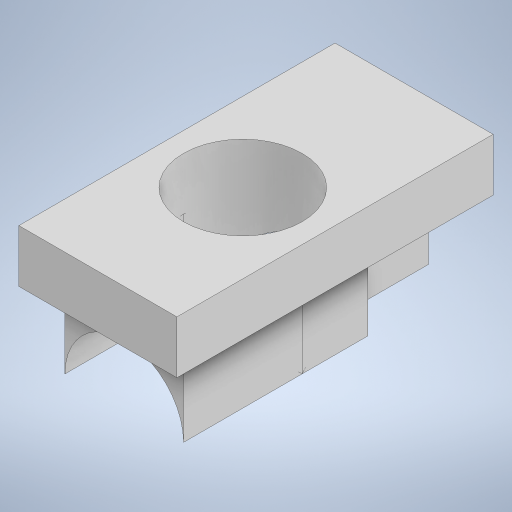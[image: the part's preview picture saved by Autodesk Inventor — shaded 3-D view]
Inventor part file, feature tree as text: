
AUTODESK INVENTOR PART (.ipt)
format: ipt  version: 2023 (Build 270158000, 158)  size: 335,872 bytes
history: native  units: in
note: dims shown in document units (in); Inventor stores cm internally (conversion verified against a paired STEP export)
features: extrude x6, plane x6, sketch x5, projected_geometry x1
ambient origin geometry x8: Origin, YZ Plane, XZ Plane, XY Plane, X Axis, Y Axis, Z Axis, Center Point
bodies: Solid1 (feature_tree)
feature tree (18):
  sketch  "Sketch1"  dims[d0=2.3622in d1=4.7244in]
  extrude  "Extrusion1"  Depth=4.7244in
  plane  "Work Plane1"
  sketch  "Sketch2"  dims[d2=1.7717in d3=0.1969in]
  plane  "Work Plane2"
  extrude  "Extrusion2"  Depth=0.1969in
  extrude  "Extrusion3"  TaperAngle=0.0deg  [1 undecoded]
  plane  "Work Plane6"
  sketch  "Sketch3"  dims[d4=0.9843in d5=0.0in]
  sketch  "Sketch4"  dims[d6=0.4921in d7=0.3937in]
  sketch  "Sketch5"  dims[d8=0.0984in d9=0.8858in d10=-2.7559in d11=0.9843in d12=90.0deg d13=0.8268in d14=0.1969in d15=0.3937in d16=90.0deg d17=0.3937in d19=-2.7559in d20=90.0deg d21=-1.378in d22=1.7717in d23=0.7874in d24=0.0in d25=2.3622in d26=2.3622in d27=1.1811in d28=1.1811in d29=0.3937in d30=0.0in d31=0.0in d32=0.0in d33=0.3937in d34=0.0in d35=0.3937in d36=0.0in d37=0.3937in d38=0.0in d39=0.0in d40=0.0in d41=0.0in d42=0.0in]
  extrude  "Extrusion4"  Depth=0.3937in
  extrude  "Extrusion5"  Depth=0.8858in
  extrude  "Extrusion6"  [1 undecoded]
  projected_geometry  "Projected Loop1"
  plane  "Work Plane3"
  plane  "Work Plane4"
  plane  "Work Plane5"
note: 2 required parameter values undecoded (feature->parameter linkage not recoverable at this tier; creation-order binding heuristic only, values carry confidence <= 0.55)
